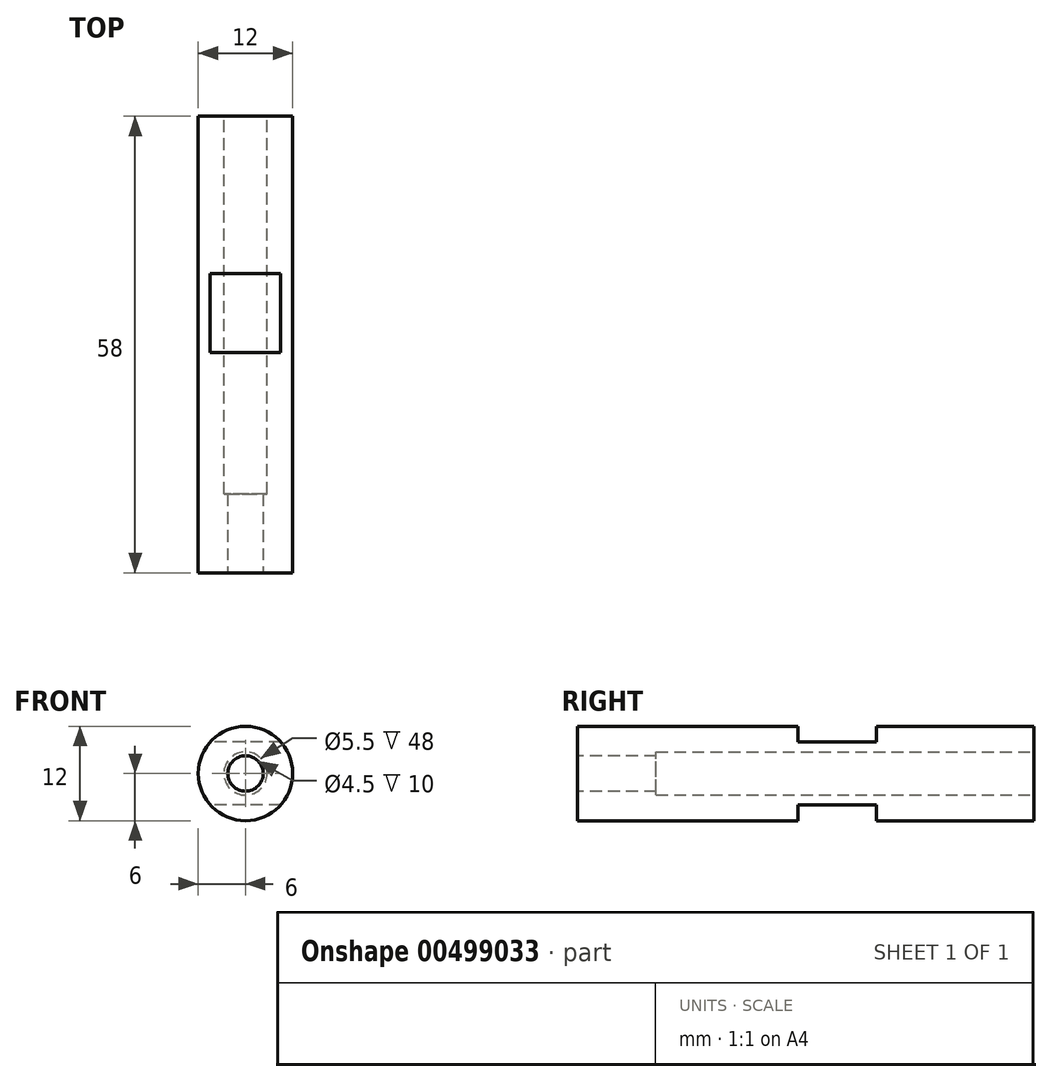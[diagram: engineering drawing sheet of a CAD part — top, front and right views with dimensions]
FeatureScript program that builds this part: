
annotation { "Feature Type Name" : "Feature", "Feature Type Description" : "" }
export const myFeature = defineFeature(function(context is Context, id is Id, definition is map)
    precondition{}
    {
        {
            var Q0;
            Q0=qCreatedBy(makeId("Front.planeOp"),FACE);
            var sketch = newSketch(context, id + "F0", { "sketchPlane" : qUnion([Q0])});
            skCircle(sketch, "E0", {"center": v(0, 0) * mm, "radius": 6 * mm});
            skSolve(sketch);
        }
        {
            var Q0;
            Q0=makeQuery(id+"F0.imprint","IMPRINT",FACE,{"disambiguationData":[TD([[makeQuery(id+"F0.imprint","IMPRINT",EDGE,{"derivedFrom":sQuery(id+"F0.wireOp",EDGE,"E0")}),1.0]])]});
            extrude(context, id + "F1", {"entities" : qUnion([Q0]), "depth" : 58 * mm});
        }
        {
            var Q0;
            Q0=qCreatedBy(makeId("Front.planeOp"),FACE);
            var sketch = newSketch(context, id + "F2", { "sketchPlane" : qUnion([Q0])});
            skCircle(sketch, "E1", {"center": v(0, 0) * mm, "radius": 2.75 * mm});
            skSolve(sketch);
        }
        {
            var Q0;
            Q0=makeQuery(id+"F2.imprint","IMPRINT",FACE,{"disambiguationData":[TD([[makeQuery(id+"F2.imprint","IMPRINT",EDGE,{"derivedFrom":sQuery(id+"F2.wireOp",EDGE,"E1")}),1.0]])]});
            var Q1;
            Q1=sQuery(id+"F2.wireOp",EDGE,"E1");
            extrude(context, id + "F3", {"entities" : qUnion([Q0]), "operationType" : NewBodyOperationType.REMOVE, "surfaceEntities" : qUnion([Q1]), "depth" : 48 * mm});
        }
        {
            var Q0;
            Q0=qCreatedBy(makeId("Right.planeOp"),FACE);
            var sketch = newSketch(context, id + "F4", { "sketchPlane" : qUnion([Q0])});
            skLineSegment(sketch, "E2", {"start": v(0, 0) * mm, "end": v(0, -6) * mm});
            skLineSegment(sketch, "E3", {"start": v(0, -6) * mm, "end": v(-20, -6) * mm});
            skLineSegment(sketch, "E4.bottom", {"start": v(-20, -6) * mm, "end": v(-30, -6) * mm});
            skLineSegment(sketch, "E4.top", {"start": v(-20, -4) * mm, "end": v(-30, -4) * mm});
            skLineSegment(sketch, "E4.left", {"start": v(-20, -6) * mm, "end": v(-20, -4) * mm});
            skLineSegment(sketch, "E4.right", {"start": v(-30, -6) * mm, "end": v(-30, -4) * mm});
            skLineSegment(sketch, "E5.bottom", {"start": v(-20, 6) * mm, "end": v(-30, 6) * mm});
            skLineSegment(sketch, "E5.top", {"start": v(-20, 4) * mm, "end": v(-30, 4) * mm});
            skLineSegment(sketch, "E5.left", {"start": v(-20, 6) * mm, "end": v(-20, 4) * mm});
            skLineSegment(sketch, "E5.right", {"start": v(-30, 6) * mm, "end": v(-30, 4) * mm});
            skSolve(sketch);
        }
        {
            var Q0;
            Q0=makeQuery(id+"F4.imprint","IMPRINT",FACE,{"disambiguationData":[TD([[makeQuery(id+"F4.imprint","IMPRINT",EDGE,{"derivedFrom":sQuery(id+"F4.wireOp",EDGE,"E4.bottom")}),-1.0]])]});
            var Q1;
            Q1=makeQuery(id+"F4.imprint","IMPRINT",FACE,{"disambiguationData":[TD([[makeQuery(id+"F4.imprint","IMPRINT",EDGE,{"derivedFrom":sQuery(id+"F4.wireOp",EDGE,"E5.bottom")}),1.0]])]});
            var Q2;
            Q2=sQuery(id+"F4.wireOp",EDGE,"E5.top");
            var Q3;
            Q3=sQuery(id+"F4.wireOp",EDGE,"E5.right");
            var Q4;
            Q4=sQuery(id+"F4.wireOp",EDGE,"E5.bottom");
            var Q5;
            Q5=sQuery(id+"F4.wireOp",EDGE,"E5.left");
            var Q6;
            Q6=sQuery(id+"F4.wireOp",EDGE,"E4.top");
            var Q7;
            Q7=sQuery(id+"F4.wireOp",EDGE,"E4.right");
            var Q8;
            Q8=sQuery(id+"F4.wireOp",EDGE,"E4.bottom");
            var Q9;
            Q9=sQuery(id+"F4.wireOp",EDGE,"E4.left");
            extrude(context, id + "F5", {"entities" : qUnion([Q0, Q1]), "operationType" : NewBodyOperationType.REMOVE, "surfaceEntities" : qUnion([Q2, Q3, Q4, Q5, Q6, Q7, Q8, Q9]), "endBound" : BoundingType.THROUGH_ALL, "depth" : 50 * mm, "hasSecondDirection" : true, "secondDirectionBound" : SecondDirectionBoundingType.THROUGH_ALL, "secondDirectionOppositeDirection" : true, "secondDirectionDepth" : 25 * mm});
        }
        {
            var Q0;
            Q0=makeQuery(id+"F1.opExtrude","CAP_FACE",FACE,{"disambiguationData":[OSD([sQuery(id+"F0.wireOp",EDGE,"E0")])],"isStart":false});
            var sketch = newSketch(context, id + "F6", { "sketchPlane" : qUnion([Q0])});
            skPoint(sketch, "E6", {"position": v(0, 0) * mm});
            skSolve(sketch);
        }
        {
            var Q0;
            Q0=sQuery(id+"F6.wireOp",VERTEX,"E6");
            var Q1;
            Q1=makeQuery(id+"F1.opExtrude","SWEPT_BODY",BODY,{"disambiguationData":[OSD([sQuery(id+"F0.wireOp",EDGE,"E0")])]});
            hole(context, id + "F7", {"style" : HoleStyle.SIMPLE, "endStyle" : HoleEndStyle.BLIND, "standardTappedOrClearance" : lookupTablePath({ "standard" : "ISO", "engagement" : "75%", "pitch" : "0.5 mm", "size" : "M5", "type" : "Tapped" }), "standardBlindInLast" : lookupTablePath({ "standard" : "ISO", "engagement" : "75%", "pitch" : "0.5 mm", "size" : "M5", "type" : "Tapped" }), "holeDiameter" : 4.5 * mm, "showTappedDepth" : true, "holeDepth" : 10 * mm, "tappedDepth" : 10 * mm, "tapClearance" : 0, "startFromSketch" : true, "locations" : qUnion([Q0]), "scope" : qUnion([Q1]), "majorDiameter" : 5 * mm});
        }
    });
